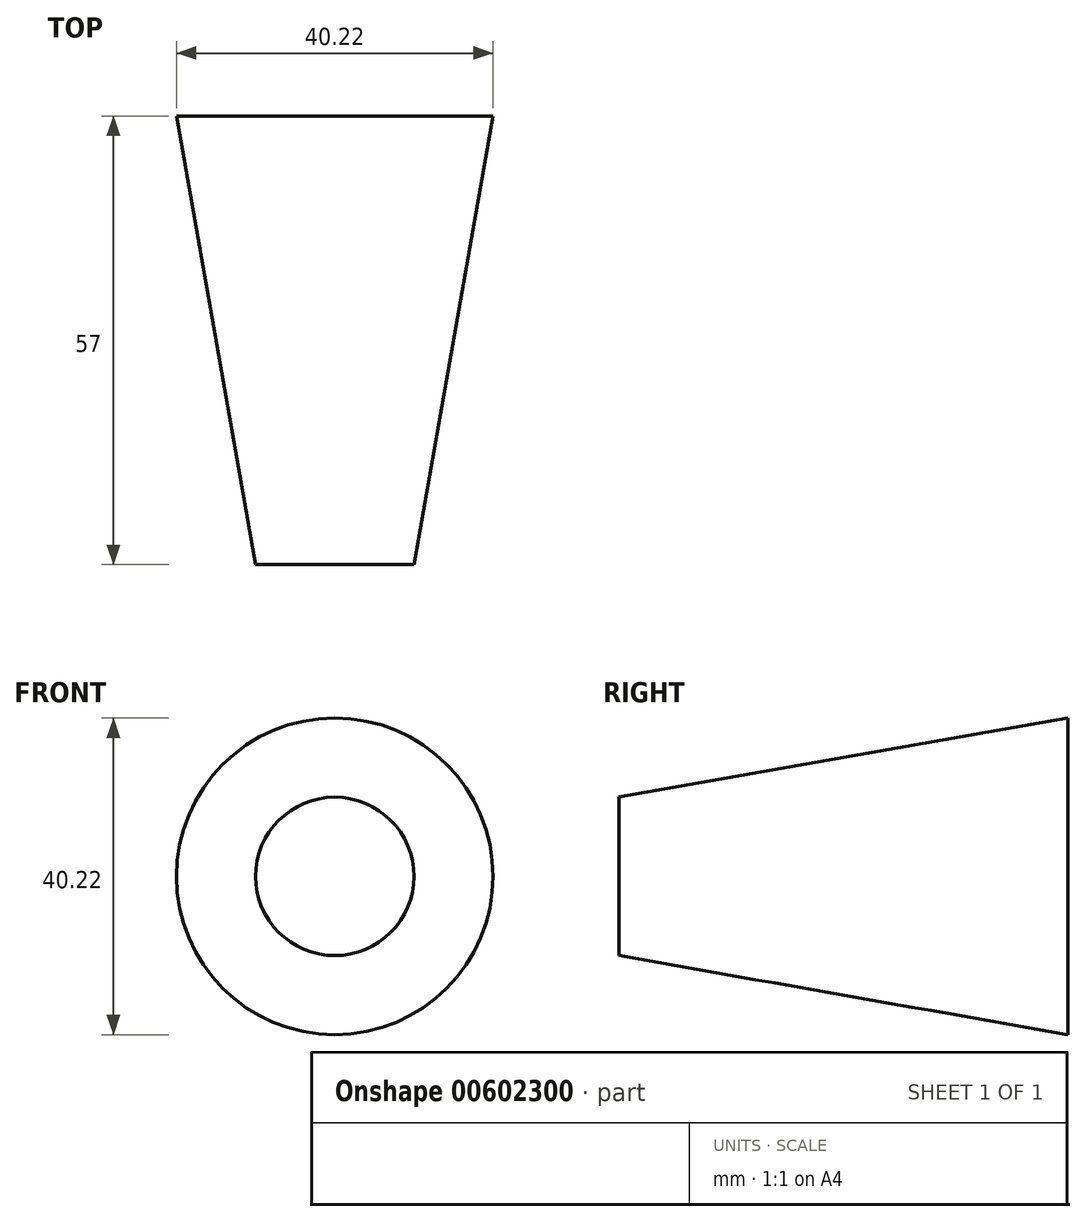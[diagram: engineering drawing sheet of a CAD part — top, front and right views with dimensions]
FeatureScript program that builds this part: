
annotation { "Feature Type Name" : "Feature", "Feature Type Description" : "" }
export const myFeature = defineFeature(function(context is Context, id is Id, definition is map)
    precondition{}
    {
        {
            var Q0;
            Q0=qCreatedBy(makeId("Front.planeOp"),FACE);
            var sketch = newSketch(context, id + "F0", { "sketchPlane" : qUnion([Q0])});
            skCircle(sketch, "E0", {"center": v(0, 0) * mm, "radius": 20.11 * mm});
            skSolve(sketch);
        }
        {
            var Q0;
            Q0=makeQuery(id+"F0.imprint","IMPRINT",FACE,{"disambiguationData":[TD([[makeQuery(id+"F0.imprint","IMPRINT",EDGE,{"derivedFrom":sQuery(id+"F0.wireOp",EDGE,"E0")}),1.0]])]});
            extrude(context, id + "F1", {"entities" : qUnion([Q0]), "depth" : 57 * mm, "offsetDistance" : 25 * mm, "hasDraft" : true, "draftAngle" : 10 * degree, "draftPullDirection" : true});
        }
    });
